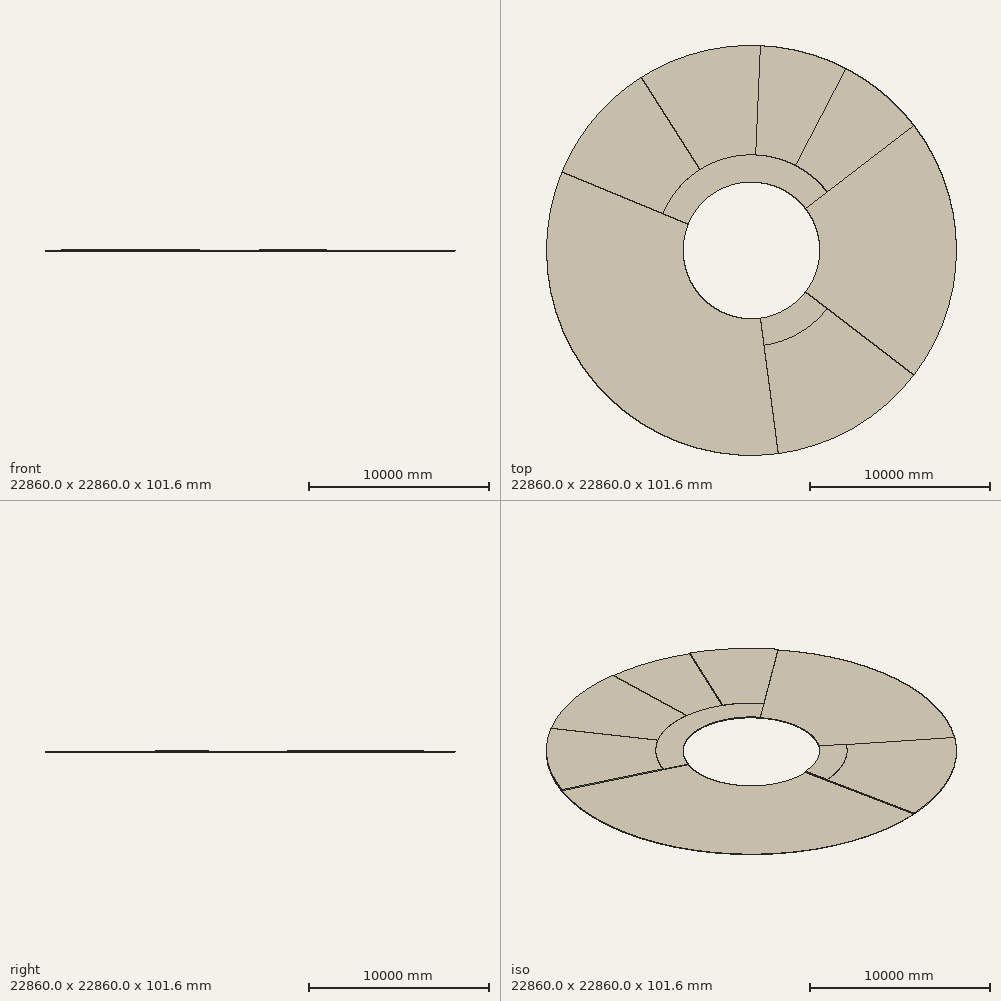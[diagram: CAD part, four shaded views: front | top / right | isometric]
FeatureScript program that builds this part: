
annotation { "Feature Type Name" : "Feature", "Feature Type Description" : "" }
export const myFeature = defineFeature(function(context is Context, id is Id, definition is map)
    precondition{}
    {
        {
            var Q0;
            Q0=qCreatedBy(makeId("Top.planeOp"),FACE);
            var sketch = newSketch(context, id + "F0", { "sketchPlane" : qUnion([Q0])});
            skCircle(sketch, "E0", {"center": v(0, 0) * mm, "radius": 3810 * mm});
            skCircle(sketch, "E1.0", {"center": v(0, 0) * mm, "radius": 11430 * mm});
            skLineSegment(sketch, "E2", {"start": v(0, 0) * mm, "end": v(4001.02, 0) * mm, "construction": true});
            skLineSegment(sketch, "E3", {"start": v(2462.97, 4731.32) * mm, "end": v(5277.79, 10138.53) * mm});
            skLineSegment(sketch, "E4", {"start": v(232.67, 5328.92) * mm, "end": v(498.57, 11419.12) * mm});
            skLineSegment(sketch, "E5", {"start": v(497.3, -3777.4) * mm, "end": v(1491.91, -11332.21) * mm});
            skLineSegment(sketch, "E6", {"start": v(-2865.96, 4498.65) * mm, "end": v(-6141.33, 9639.96) * mm});
            skLineSegment(sketch, "E7", {"start": v(3022.68, 2319.38) * mm, "end": v(9068.03, 6958.14) * mm});
            skLineSegment(sketch, "E8", {"start": v(3022.68, -2319.38) * mm, "end": v(9068.03, -6958.14) * mm});
            skArc(sketch, "E9.0", {"start": v(4231.75, 3247.13) * mm, "mid": v(-696.23, 5288.37) * mm, "end": v(-4927.97, 2041.23) * mm});
            skLineSegment(sketch, "E10", {"start": v(5433.2, 350.82) * mm, "end": v(4755.58, 2212.54) * mm, "construction": true});
            skLineSegment(sketch, "E11", {"start": v(4755.58, 2212.54) * mm, "end": v(9338.27, 3880.5) * mm, "construction": true});
            skLineSegment(sketch, "E12", {"start": v(9338.27, 3880.5) * mm, "end": v(10015.88, 2018.79) * mm, "construction": true});
            skLineSegment(sketch, "E13", {"start": v(10015.88, 2018.79) * mm, "end": v(5433.2, 350.82) * mm, "construction": true});
            skLineSegment(sketch, "E14.MirrorCS", {"start": v(9338.27, -3880.5) * mm, "end": v(10015.88, -2018.79) * mm, "construction": true});
            skLineSegment(sketch, "E15.MirrorCS", {"start": v(4755.58, -2212.54) * mm, "end": v(9338.27, -3880.5) * mm, "construction": true});
            skLineSegment(sketch, "E16.MirrorCS", {"start": v(5433.2, -350.82) * mm, "end": v(4755.58, -2212.54) * mm, "construction": true});
            skLineSegment(sketch, "E17.MirrorCS", {"start": v(10015.88, -2018.79) * mm, "end": v(5433.2, -350.82) * mm, "construction": true});
            skLineSegment(sketch, "E18", {"start": v(-10559.94, 4374.07) * mm, "end": v(-3519.98, 1458.02) * mm});
            skLineSegment(sketch, "E19", {"start": v(3022.68, 2319.38) * mm, "end": v(3022.68, -2319.38) * mm, "construction": true});
            skArc(sketch, "E20.0", {"start": v(696.23, -5288.37) * mm, "mid": v(2667, -4619.38) * mm, "end": v(4231.75, -3247.13) * mm});
            skPoint(sketch, "E21", {"position": v(6045.35, -4638.76) * mm});
            skPoint(sketch, "E22", {"position": v(6045.35, 4638.76) * mm});
            skSolve(sketch);
        }
        {
            var Q0;
            {var subQ6=sQuery(id+"F0.wireOp",EDGE,"E8");Q0=makeQuery(id+"F0.imprint","IMPRINT",FACE,{"disambiguationData":[TD([[makeQuery(id+"F0.imprint","IMPRINT",EDGE,{"derivedFrom":subQ6}),1.0]])]});}
            var Q1;
            {var subQ4=sQuery(id+"F0.wireOp",EDGE,"E5");Q1=makeQuery(id+"F0.imprint","IMPRINT",FACE,{"disambiguationData":[TD([[makeQuery(id+"F0.imprint","IMPRINT",EDGE,{"derivedFrom":subQ4}),-1.0]])]});}
            var Q2;
            {var subQ0=sQuery(id+"F0.wireOp",EDGE,"E3");Q2=makeQuery(id+"F0.imprint","IMPRINT",FACE,{"disambiguationData":[TD([[makeQuery(id+"F0.imprint","IMPRINT",EDGE,{"derivedFrom":subQ0}),1.0]])]});}
            extrude(context, id + "F1", {"entities" : qUnion([Q0, Q1, Q2]), "depth" : 25.4 * mm, "offsetDistance" : 25.4 * mm});
        }
        {
            var Q0;
            {var subQ0=sQuery(id+"F0.wireOp",EDGE,"E4");Q0=makeQuery(id+"F0.imprint","IMPRINT",FACE,{"disambiguationData":[TD([[makeQuery(id+"F0.imprint","IMPRINT",EDGE,{"derivedFrom":subQ0}),1.0]])]});}
            var Q1;
            {var subQ0=sQuery(id+"F0.wireOp",EDGE,"E3");Q1=makeQuery(id+"F0.imprint","IMPRINT",FACE,{"disambiguationData":[TD([[makeQuery(id+"F0.imprint","IMPRINT",EDGE,{"derivedFrom":subQ0}),-1.0]])]});}
            var Q2;
            {var subQ5=sQuery(id+"F0.wireOp",EDGE,"E20.0");Q2=makeQuery(id+"F0.imprint","IMPRINT",FACE,{"disambiguationData":[TD([[makeQuery(id+"F0.imprint","IMPRINT",EDGE,{"derivedFrom":subQ5}),-1.0]])]});}
            extrude(context, id + "F2", {"entities" : qUnion([Q0, Q1, Q2]), "depth" : 76.2 * mm, "offsetDistance" : 25.4 * mm});
        }
        {
            var Q0;
            {var subQ4=sQuery(id+"F0.wireOp",EDGE,"E6");var subQ5=sQuery(id+"F0.wireOp",EDGE,"E0");var subQ6=makeQuery(id+"F0.imprint","INTERSECT",VERTEX,{"derivedFrom":[subQ5,subQ4]});Q0=makeQuery(id+"F0.imprint","IMPRINT",FACE,{"disambiguationData":[TD([[makeQuery(id+"F0.imprint","IMPRINT",EDGE,{"disambiguationData":[TD([[subQ6,1.0]])],"derivedFrom":subQ5}),-1.0]])]});}
            var Q1;
            {var subQ0=sQuery(id+"F0.wireOp",EDGE,"E6");Q1=makeQuery(id+"F0.imprint","IMPRINT",FACE,{"disambiguationData":[TD([[makeQuery(id+"F0.imprint","IMPRINT",EDGE,{"derivedFrom":subQ0}),1.0]])]});}
            extrude(context, id + "F3", {"entities" : qUnion([Q0, Q1]), "depth" : 101.6 * mm, "offsetDistance" : 25.4 * mm});
        }
        {
            var Q0;
            {var subQ3=sQuery(id+"F0.wireOp",EDGE,"E7");var subQ5=sQuery(id+"F0.wireOp",EDGE,"E0");var subQ6=makeQuery(id+"F0.imprint","INTERSECT",VERTEX,{"derivedFrom":[subQ5,subQ3]});Q0=makeQuery(id+"F0.imprint","IMPRINT",FACE,{"disambiguationData":[TD([[makeQuery(id+"F0.imprint","IMPRINT",EDGE,{"disambiguationData":[TD([[subQ6,-1.0]])],"derivedFrom":subQ5}),-1.0]])]});}
            extrude(context, id + "F4", {"entities" : qUnion([Q0]), "depth" : 60.96 * mm, "offsetDistance" : 30.48 * mm});
        }
    });
